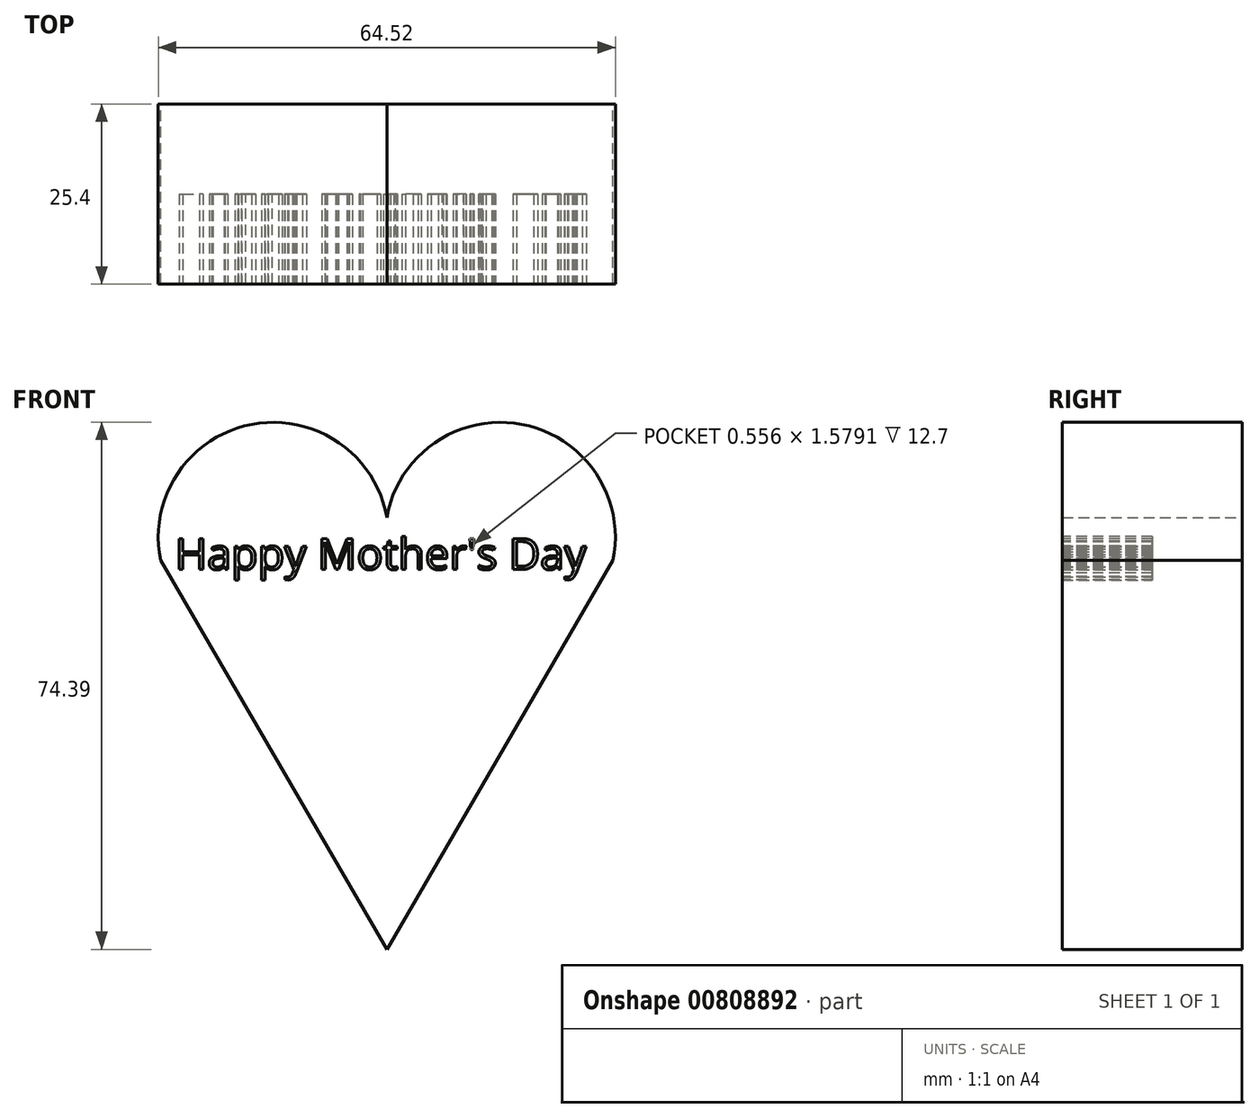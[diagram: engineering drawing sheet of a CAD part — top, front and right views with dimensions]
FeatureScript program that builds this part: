
annotation { "Feature Type Name" : "Feature", "Feature Type Description" : "" }
export const myFeature = defineFeature(function(context is Context, id is Id, definition is map)
    precondition{}
    {
        {
            var Q0;
            Q0=qCreatedBy(makeId("Front.planeOp"),FACE);
            var sketch = newSketch(context, id + "F0", { "sketchPlane" : qUnion([Q0])});
            skLineSegment(sketch, "E0", {"start": v(0, -33.47) * mm, "end": v(-31.94, 21.42) * mm});
            skLineSegment(sketch, "E1", {"start": v(0, -33.47) * mm, "end": v(31.94, 21.42) * mm});
            skLineSegment(sketch, "E2", {"start": v(0, -33.47) * mm, "end": v(0, 21.83) * mm});
            skArc(sketch, "E3", {"start": v(0, 21.83) * mm, "mid": v(-16.22, 40.92) * mm, "end": v(-31.94, 21.42) * mm});
            skArc(sketch, "E4", {"start": v(31.94, 21.42) * mm, "mid": v(16.22, 40.92) * mm, "end": v(0, 21.83) * mm});
            skSolve(sketch);
        }
        {
            var Q0;
            Q0 = qSketchRegion(id + "F0", true);
            extrude(context, id + "F1", {"entities" : qUnion([Q0]), "depth" : 25.4 * mm, "offsetDistance" : 25.4 * mm});
        }
        {
            var Q0;
            Q0=makeQuery(id+"F1.opExtrude","CAP_FACE",FACE,{"disambiguationData":[OSD([sQuery(id+"F0.wireOp",EDGE,"E0"),sQuery(id+"F0.wireOp",EDGE,"E1"),sQuery(id+"F0.wireOp",EDGE,"E3"),sQuery(id+"F0.wireOp",EDGE,"E4")])],"isStart":false});
            var sketch = newSketch(context, id + "F2", { "sketchPlane" : qUnion([Q0])});
            skText(sketch, "E5", { "text": "Happy Mother\'s Day", "fontName": "OpenSans-Regular.ttf"});
            const initialGuessF2  = {"E5": [-0.02988, 0.02014, 1, 0, 0.00441]};
            skSetInitialGuess(sketch, initialGuessF2);
            skSolve(sketch);
        }
        {
            var Q0;
            Q0 = qSketchRegion(id + "F2", true);
            extrude(context, id + "F3", {"entities" : qUnion([Q0]), "operationType" : NewBodyOperationType.REMOVE, "oppositeDirection" : true, "depth" : 12.7 * mm, "offsetDistance" : 25.4 * mm});
        }
    });
